# Revit family: Table-Teknion-Zones_ZNTWC-R2015
name_source: partatom
category: Furniture
revit_build: Autodesk Revit Architecture 2015 (Build: 20140322_1515(x64)
units: mm (PartAtom-declared; Revit-internal decimal feet)

## types (2) — shared parameters
Assembly Code = E2020200
Depth = 48"
Height = 16"
Manufacturer = Teknion
Manufacturer Fax = 416.661.4586
Number of Poles = 1
Part Number = ZNTWC
Product Documentation Link = http://www.teknion.com
Product Line = Zones
Product Page URL = http://www.teknion.com
Series = Zones
Sustainability Data = http://www.teknion.com
Table Diameter = 48"
URL = http://www.teknion.com
Warranty = http://www.teknion.com
Width = 48"

## per-type parameters (varying)
| type | Description | Model | With Power Pill |
| Table 48", with Power Pill | Round Lounge Workshop Table, 48"dia, with Center Pill Cut-Out | ZNTWC48P | Yes |
| Table 48" | Round Lounge Workshop Table, 48"dia, without Cut-Out | ZNTWC48N | No |

## geometry (parser evidence)
native form markers: Blend x153, Sweep x8
no freeform markers — native parametric forms only
